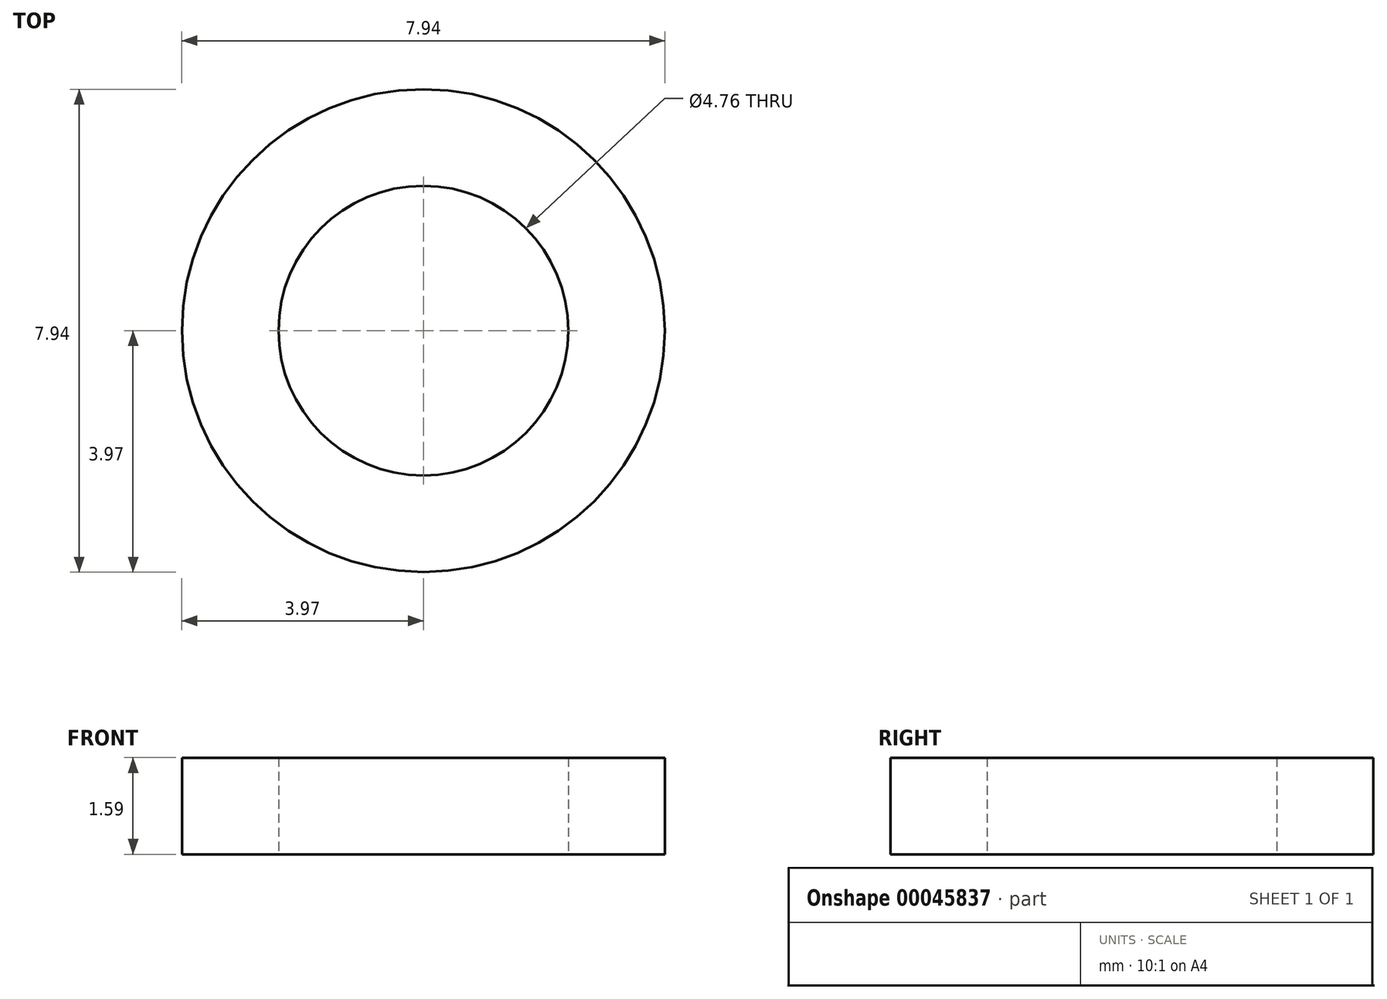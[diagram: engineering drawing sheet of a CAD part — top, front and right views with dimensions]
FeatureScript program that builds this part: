
annotation { "Feature Type Name" : "Feature", "Feature Type Description" : "" }
export const myFeature = defineFeature(function(context is Context, id is Id, definition is map)
    precondition{}
    {
        {
            var Q0;
            Q0=qCreatedBy(makeId("Top.planeOp"),FACE);
            var sketch = newSketch(context, id + "F0", { "sketchPlane" : qUnion([Q0])});
            skCircle(sketch, "E0", {"center": v(0, 0) * mm, "radius": 2.38 * mm});
            skCircle(sketch, "E1", {"center": v(0, 0) * mm, "radius": 3.97 * mm});
            skSolve(sketch);
        }
        {
            var Q0;
            Q0=qSketchRegion(id+"F0",true);
            extrude(context, id + "F1", {"entities" : qUnion([Q0]), "depth" : 1.59 * mm});
        }
    });
